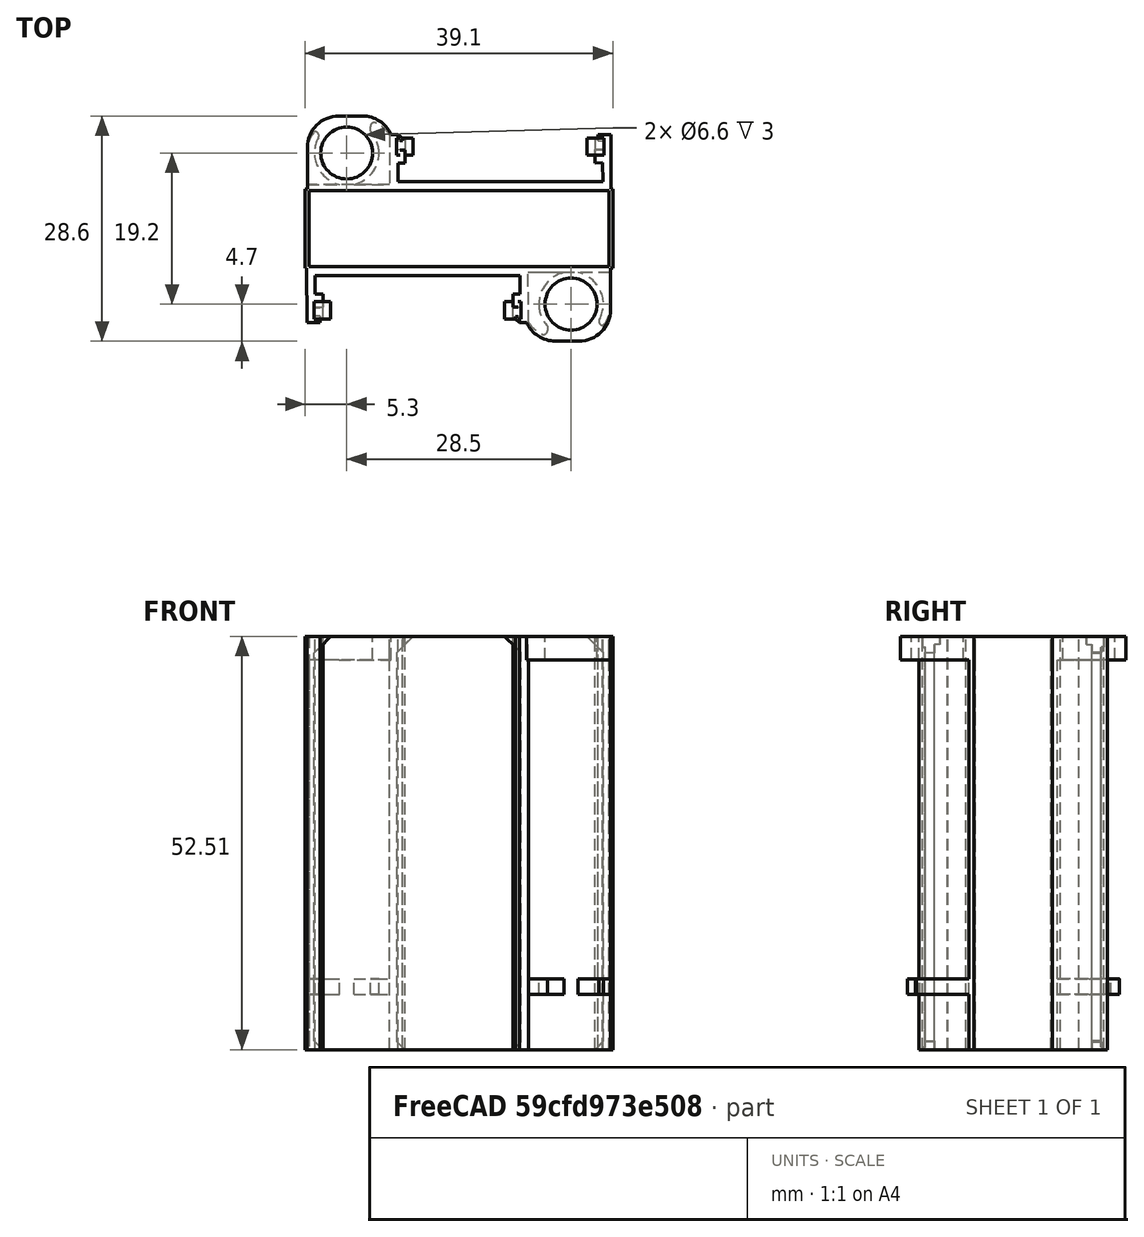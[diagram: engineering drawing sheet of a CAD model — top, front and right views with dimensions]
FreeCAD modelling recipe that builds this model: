
FCSTD DOCUMENT  (FreeCAD 0.18.4R)
Label: ArduinoClip3
License: All rights reserved
LicenseURL: http://en.wikipedia.org/wiki/All_rights_reserved
objects: Part::Fillet×12, Sketcher::SketchObject×10, PartDesign::Pad×10, Part::Box×10, Part::Cut×6, Part::Cylinder×4, Part::MultiFuse×3, Mesh::Feature×1
note: 65 computed .brp shape members not serialized (recipe doc carries the construction recipe); baked Part::Feature solids carry a one-line shape summary decoded from their .brp

FEATURE [Sketcher::SketchObject] Sketch
  MapMode = 5
  sketch-geometry (21):
    g0: LineSegment StartX=-18.4968 StartY=-10.0088 StartZ=0 EndX=7.53504 EndY=-10.0088 EndZ=0
    g1: LineSegment StartX=8.57388 StartY=-11.2005 StartZ=0 EndX=-19.5534 EndY=-11.2005 EndZ=0
    g2: LineSegment StartX=-17.6048 StartY=-6.00567 StartZ=0 EndX=-17.6048 EndY=-7.68179 EndZ=0
    g3: LineSegment StartX=8.57269 StartY=-4.05913 StartZ=0 EndX=8.57388 EndY=-11.2005 EndZ=0
    g4: LineSegment StartX=6.91065 StartY=-4.05913 StartZ=0 EndX=6.91356 EndY=-4.85559 EndZ=0
    g5: LineSegment StartX=6.91065 StartY=-4.05913 StartZ=0 EndX=8.57269 EndY=-4.05913 EndZ=0
    g6: LineSegment StartX=6.91356 StartY=-4.85559 StartZ=0 EndX=7.6386 EndY=-4.86736 EndZ=0
    g7: LineSegment StartX=7.6386 StartY=-4.86736 StartZ=0 EndX=7.64142 EndY=-5.99166 EndZ=0
    g8: LineSegment StartX=7.64142 StartY=-5.99166 StartZ=0 EndX=6.53466 EndY=-5.99604 EndZ=0
    g9: LineSegment StartX=6.53466 StartY=-5.99604 StartZ=0 EndX=6.53538 EndY=-7.65721 EndZ=0
    g10: LineSegment StartX=-17.6048 StartY=-6.00567 StartZ=0 EndX=-18.6255 EndY=-6.00154 EndZ=0
    g11: LineSegment StartX=-18.6255 StartY=-6.00154 StartZ=0 EndX=-18.62 EndY=-4.8031 EndZ=0
    g12: LineSegment StartX=-18.62 StartY=-4.8031 StartZ=0 EndX=-17.9262 EndY=-4.80553 EndZ=0
    g13: LineSegment StartX=-17.9262 StartY=-4.80553 StartZ=0 EndX=-17.9262 EndY=-4.48409 EndZ=0
    g14: LineSegment StartX=-17.9262 StartY=-4.48409 StartZ=0 EndX=-18.4601 EndY=-4.05553 EndZ=0
    g15: LineSegment StartX=-19.5659 StartY=-4.05361 StartZ=0 EndX=-19.5534 EndY=-11.2005 EndZ=0
    g16: LineSegment StartX=-17.6048 StartY=-7.68179 StartZ=0 EndX=-18.4968 EndY=-7.686 EndZ=0
    g17: LineSegment StartX=-18.4968 StartY=-7.686 StartZ=0 EndX=-18.4968 EndY=-10.0088 EndZ=0
    g18: LineSegment StartX=7.5169 StartY=-7.64985 StartZ=0 EndX=6.53538 EndY=-7.65721 EndZ=0
    g19: LineSegment StartX=7.53504 StartY=-10.0088 StartZ=0 EndX=7.5169 EndY=-7.64985 EndZ=0
    g20: LineSegment StartX=-19.5659 StartY=-4.05361 StartZ=0 EndX=-18.4601 EndY=-4.05553 EndZ=0
  constraints (24):
    c: Horizontal(g0)
    c: Horizontal(g1)
    c: Vertical(g2)
    c: Coincident(g1,g3)
    c: Coincident(g5,g4)
    c: Coincident(g4,g6)
    c: Coincident(g6,g7)
    c: Coincident(g7,g8)
    c: Coincident(g9,g8)
    c: Coincident(g5,g3)
    c: Coincident(g10,g2)
    c: Coincident(g10,g11)
    c: Coincident(g11,g12)
    c: Coincident(g12,g13)
    c: Coincident(g13,g14)
    c: Coincident(g15,g1)
    c: Coincident(g16,g2)
    c: Coincident(g16,g17)
    c: Coincident(g0,g17)
    c: Coincident(g9,g18)
    c: Coincident(g18,g19)
    c: Coincident(g0,g19)
    c: Coincident(g20,g15)
    c: Coincident(g20,g14)
FEATURE [PartDesign::Pad] Pad
  Length = 52.5
  Length2 = 100
  Profile = -> Sketch
  Type = 0
FEATURE [Sketcher::SketchObject] Sketch004
  MapMode = 5
  Placement = pos=(-11.64,-4.5,6.03) rot=(1,0,0;1.5708rad)
  sketch-geometry (3):
    g0: LineSegment StartX=-7.00166 StartY=-5.01077 StartZ=0 EndX=-6.98953 EndY=-6.02972 EndZ=0
    g1: LineSegment StartX=-6.98953 StartY=-6.02972 StartZ=0 EndX=-5.96627 EndY=-6.02972 EndZ=0
    g2: LineSegment StartX=-7.00166 StartY=-5.01077 StartZ=0 EndX=-5.96627 EndY=-6.02972 EndZ=0
  constraints (3):
    c: Coincident(g0,g1)
    c: Coincident(g2,g0)
    c: Coincident(g2,g1)
FEATURE [PartDesign::Pad] Pad004  label="stopper002"
  Length = 2.2
  Length2 = 100
  Placement = pos=(-11.64,-4.5,6.03) rot=(1,0,0;1.5708rad)
  Profile = -> Sketch004
  Type = 0
FEATURE [Sketcher::SketchObject] Sketch006
  MapMode = 5
  Placement = pos=(7.7,-4.5,0.03) rot=(1,0,0;1.5708rad)
  sketch-geometry (3):
    g0: LineSegment StartX=-0.009992 StartY=1.14657 StartZ=0 EndX=-0.005347 EndY=-0.027131 EndZ=0
    g1: LineSegment StartX=-0.005347 StartY=-0.027131 StartZ=0 EndX=-1.16636 EndY=-0.03134 EndZ=0
    g2: LineSegment StartX=-1.16636 StartY=-0.03134 StartZ=0 EndX=-0.009992 EndY=1.14657 EndZ=0
  constraints (3):
    c: Coincident(g0,g1)
    c: Coincident(g1,g2)
    c: Coincident(g2,g0)
FEATURE [PartDesign::Pad] Pad006  label="stopper003"
  Length = 2.2
  Length2 = 100
  Placement = pos=(7.7,-4.5,0.03) rot=(1,0,0;1.5708rad)
  Profile = -> Sketch006
  Type = 0
FEATURE [Sketcher::SketchObject] Sketch007
  MapMode = 5
  Placement = pos=(7.66,-4.5,50.5) rot=(1,0,0;1.5708rad)
  sketch-geometry (3):
    g0: LineSegment StartX=0.006942 StartY=2.00104 StartZ=0 EndX=-0.00277 EndY=-0.125835 EndZ=0
    g1: LineSegment StartX=-0.00277 StartY=-0.125835 StartZ=0 EndX=-2.12965 EndY=2.01075 EndZ=0
    g2: LineSegment StartX=-2.12965 StartY=2.01075 StartZ=0 EndX=0.006942 EndY=2.00104 EndZ=0
  constraints (3):
    c: Coincident(g0,g1)
    c: Coincident(g1,g2)
    c: Coincident(g2,g0)
FEATURE [Sketcher::SketchObject] Sketch008
  MapMode = 5
  Placement = pos=(-17.65,-4.5,50.5) rot=(1,0,0;1.5708rad)
  sketch-geometry (3):
    g0: LineSegment StartX=1.0898 StartY=1.99523 StartZ=0 EndX=-0.993398 EndY=-0.061924 EndZ=0
    g1: LineSegment StartX=-0.993398 StartY=-0.061924 StartZ=0 EndX=-0.997928 EndY=2.00119 EndZ=0
    g2: LineSegment StartX=-0.997928 StartY=2.00119 StartZ=0 EndX=1.0898 EndY=1.99523 EndZ=0
  constraints (3):
    c: Coincident(g0,g1)
    c: Coincident(g1,g2)
    c: Coincident(g2,g0)
FEATURE [PartDesign::Pad] Pad008  label="stopper001"
  Length = 2.2
  Length2 = 100
  Placement = pos=(-17.65,-4.5,50.5) rot=(1,0,0;1.5708rad)
  Profile = -> Sketch008
  Type = 0
FEATURE [Part::Box] Box002  label="Würfel"
  AttacherType = Attacher::AttachEngine3D
  Height = 2
  Length = 11
  Placement = pos=(-30,-11,7) rot=(0,0,1;0rad)
  Width = 9
FEATURE [Part::Cylinder] Cylinder  label="Zylinder"
  Angle = 360
  AttacherType = Attacher::AttachEngine3D
  Height = 10
  Placement = pos=(-25,-6.2,0) rot=(0,0,1;0rad)
  Radius = 4.1
FEATURE [Part::Cut] Cut002
  Base = -> Box002
  Tool = -> Cylinder
FEATURE [Part::Fillet] Fillet002
  Base = -> Cut002
  Edges = 1 edges r=4: [Edge12]
FEATURE [Part::Fillet] Fillet003  label="Antenne001"
  Base = -> Fillet002
  Edges = 1 edges r=4: [Edge9]
  Placement = pos=(0,-0.2,0) rot=(0,0,1;0rad)
FEATURE [PartDesign::Pad] Pad007  label="stopper004"
  Length = 2.2
  Length2 = 100
  Placement = pos=(7.66,-4.5,50.5) rot=(1,0,0;1.5708rad)
  Profile = -> Sketch007
  Type = 0
FEATURE [Part::Box] Box003  label="Würfel001"
  AttacherType = Attacher::AttachEngine3D
  Height = 3
  Length = 11
  Placement = pos=(-30,-11,7) rot=(0,0,1;0rad)
  Width = 9.5
FEATURE [Part::Cylinder] Cylinder001  label="Zylinder001"
  Angle = 360
  AttacherType = Attacher::AttachEngine3D
  Height = 10
  Placement = pos=(-25,-6.2,0) rot=(0,0,1;0rad)
  Radius = 3.3
FEATURE [Part::Cut] Cut003
  Base = -> Box003
  Placement = pos=(0,0,42.5) rot=(0,0,1;0rad)
  Tool = -> Cylinder001
FEATURE [Part::Fillet] Fillet004
  Base = -> Cut003
  Edges = 1 edges r=4: [Edge12]
FEATURE [Part::Fillet] Fillet005  label="Antenne002"
  Base = -> Fillet004
  Edges = 1 edges r=4: [Edge9]
  Placement = pos=(0,-0.2,0) rot=(0,0,1;0rad)
FEATURE [Part::Box] Box  label="AntenneBoden"
  AttacherType = Attacher::AttachEngine3D
  Height = 50
  Length = 11
  Placement = pos=(-30,-11.2,0) rot=(0,0,1;0rad)
  Width = 0.8
FEATURE [Part::Box] Box004  label="Würfel003"
  AttacherType = Attacher::AttachEngine3D
  Height = 5
  Length = 8
  Placement = pos=(-30,-3.7,6.5) rot=(0,0,1;0rad)
  Width = 5
FEATURE [Part::Cut] Cut
  Base = -> Fillet003
  Tool = -> Box004
FEATURE [Part::Fillet] Fillet
  Base = -> Cut
  Edges = 1 edges r=0.5: [Edge12]
FEATURE [Part::Fillet] Fillet006
  Base = -> Fillet
  Edges = 1 edges r=0.5: [Edge26]
FEATURE [Part::MultiFuse] Fusion
  Shapes = -> [Pad,Fillet005,Pad004,Pad006,Pad008,Pad007,Box,Fillet006]
FEATURE [Part::Box] Box005  label="Würfel004"
  AttacherType = Attacher::AttachEngine3D
  Height = 2
  Length = 11
  Placement = pos=(-30,-11,7) rot=(0,0,1;0rad)
  Width = 9
FEATURE [Sketcher::SketchObject] Sketch009
  MapMode = 5
  Placement = pos=(-11.64,-4.5,6.03) rot=(1,0,0;1.5708rad)
  sketch-geometry (3):
    g0: LineSegment StartX=-7.00166 StartY=-5.01077 StartZ=0 EndX=-6.98953 EndY=-6.02972 EndZ=0
    g1: LineSegment StartX=-6.98953 StartY=-6.02972 StartZ=0 EndX=-5.96627 EndY=-6.02972 EndZ=0
    g2: LineSegment StartX=-7.00166 StartY=-5.01077 StartZ=0 EndX=-5.96627 EndY=-6.02972 EndZ=0
  constraints (3):
    c: Coincident(g0,g1)
    c: Coincident(g2,g0)
    c: Coincident(g2,g1)
FEATURE [PartDesign::Pad] Pad010  label="stopper005"
  Length = 2.2
  Length2 = 100
  Placement = pos=(-11.64,-4.5,6.03) rot=(1,0,0;1.5708rad)
  Profile = -> Sketch009
  Type = 0
FEATURE [Sketcher::SketchObject] Sketch010
  MapMode = 5
  Placement = pos=(7.7,-4.5,0.03) rot=(1,0,0;1.5708rad)
  sketch-geometry (3):
    g0: LineSegment StartX=-0.009992 StartY=1.14657 StartZ=0 EndX=-0.005347 EndY=-0.027131 EndZ=0
    g1: LineSegment StartX=-0.005347 StartY=-0.027131 StartZ=0 EndX=-1.16636 EndY=-0.03134 EndZ=0
    g2: LineSegment StartX=-1.16636 StartY=-0.03134 StartZ=0 EndX=-0.009992 EndY=1.14657 EndZ=0
  constraints (3):
    c: Coincident(g0,g1)
    c: Coincident(g1,g2)
    c: Coincident(g2,g0)
FEATURE [PartDesign::Pad] Pad011  label="stopper006"
  Length = 2.2
  Length2 = 100
  Placement = pos=(7.7,-4.5,0.03) rot=(1,0,0;1.5708rad)
  Profile = -> Sketch010
  Type = 0
FEATURE [Part::Box] Box006  label="Würfel005"
  AttacherType = Attacher::AttachEngine3D
  Height = 3
  Length = 11
  Placement = pos=(-30,-11,7) rot=(0,0,1;0rad)
  Width = 9.5
FEATURE [Part::Box] Box007  label="AntenneBoden001"
  AttacherType = Attacher::AttachEngine3D
  Height = 50
  Length = 11
  Placement = pos=(-30,-11.2,0) rot=(0,0,1;0rad)
  Width = 0.8
FEATURE [Sketcher::SketchObject] Sketch011
  MapMode = 5
  Placement = pos=(7.66,-4.5,50.5) rot=(1,0,0;1.5708rad)
  sketch-geometry (3):
    g0: LineSegment StartX=0.006942 StartY=2.00104 StartZ=0 EndX=-0.00277 EndY=-0.125835 EndZ=0
    g1: LineSegment StartX=-0.00277 StartY=-0.125835 StartZ=0 EndX=-2.12965 EndY=2.01075 EndZ=0
    g2: LineSegment StartX=-2.12965 StartY=2.01075 StartZ=0 EndX=0.006942 EndY=2.00104 EndZ=0
  constraints (3):
    c: Coincident(g0,g1)
    c: Coincident(g1,g2)
    c: Coincident(g2,g0)
FEATURE [PartDesign::Pad] Pad013  label="stopper008"
  Length = 2.2
  Length2 = 100
  Placement = pos=(7.66,-4.5,50.5) rot=(1,0,0;1.5708rad)
  Profile = -> Sketch011
  Type = 0
FEATURE [Part::Box] Box008  label="Würfel006"
  AttacherType = Attacher::AttachEngine3D
  Height = 5
  Length = 8
  Placement = pos=(-30,-3.7,6.5) rot=(0,0,1;0rad)
  Width = 5
FEATURE [Sketcher::SketchObject] Sketch012
  MapMode = 5
  sketch-geometry (21):
    g0: LineSegment StartX=-18.4968 StartY=-10.0088 StartZ=0 EndX=7.53504 EndY=-10.0088 EndZ=0
    g1: LineSegment StartX=8.57388 StartY=-11.2005 StartZ=0 EndX=-19.5534 EndY=-11.2005 EndZ=0
    g2: LineSegment StartX=-17.6048 StartY=-6.00567 StartZ=0 EndX=-17.6048 EndY=-7.68179 EndZ=0
    g3: LineSegment StartX=8.57269 StartY=-4.05913 StartZ=0 EndX=8.57388 EndY=-11.2005 EndZ=0
    g4: LineSegment StartX=6.91065 StartY=-4.05913 StartZ=0 EndX=6.91356 EndY=-4.85559 EndZ=0
    g5: LineSegment StartX=6.91065 StartY=-4.05913 StartZ=0 EndX=8.57269 EndY=-4.05913 EndZ=0
    g6: LineSegment StartX=6.91356 StartY=-4.85559 StartZ=0 EndX=7.6386 EndY=-4.86736 EndZ=0
    g7: LineSegment StartX=7.6386 StartY=-4.86736 StartZ=0 EndX=7.64142 EndY=-5.99166 EndZ=0
    g8: LineSegment StartX=7.64142 StartY=-5.99166 StartZ=0 EndX=6.53466 EndY=-5.99604 EndZ=0
    g9: LineSegment StartX=6.53466 StartY=-5.99604 StartZ=0 EndX=6.53538 EndY=-7.65721 EndZ=0
    g10: LineSegment StartX=-17.6048 StartY=-6.00567 StartZ=0 EndX=-18.6255 EndY=-6.00154 EndZ=0
    g11: LineSegment StartX=-18.6255 StartY=-6.00154 StartZ=0 EndX=-18.62 EndY=-4.8031 EndZ=0
    g12: LineSegment StartX=-18.62 StartY=-4.8031 StartZ=0 EndX=-17.9262 EndY=-4.80553 EndZ=0
    g13: LineSegment StartX=-17.9262 StartY=-4.80553 StartZ=0 EndX=-17.9262 EndY=-4.48409 EndZ=0
    g14: LineSegment StartX=-17.9262 StartY=-4.48409 StartZ=0 EndX=-18.4601 EndY=-4.05553 EndZ=0
    g15: LineSegment StartX=-19.5659 StartY=-4.05361 StartZ=0 EndX=-19.5534 EndY=-11.2005 EndZ=0
    g16: LineSegment StartX=-17.6048 StartY=-7.68179 StartZ=0 EndX=-18.4968 EndY=-7.686 EndZ=0
    g17: LineSegment StartX=-18.4968 StartY=-7.686 StartZ=0 EndX=-18.4968 EndY=-10.0088 EndZ=0
    g18: LineSegment StartX=7.5169 StartY=-7.64985 StartZ=0 EndX=6.53538 EndY=-7.65721 EndZ=0
    g19: LineSegment StartX=7.53504 StartY=-10.0088 StartZ=0 EndX=7.5169 EndY=-7.64985 EndZ=0
    g20: LineSegment StartX=-19.5659 StartY=-4.05361 StartZ=0 EndX=-18.4601 EndY=-4.05553 EndZ=0
  constraints (24):
    c: Horizontal(g0)
    c: Horizontal(g1)
    c: Vertical(g2)
    c: Coincident(g1,g3)
    c: Coincident(g5,g4)
    c: Coincident(g4,g6)
    c: Coincident(g6,g7)
    c: Coincident(g7,g8)
    c: Coincident(g9,g8)
    c: Coincident(g5,g3)
    c: Coincident(g10,g2)
    c: Coincident(g10,g11)
    c: Coincident(g11,g12)
    c: Coincident(g12,g13)
    c: Coincident(g13,g14)
    c: Coincident(g15,g1)
    c: Coincident(g16,g2)
    c: Coincident(g16,g17)
    c: Coincident(g0,g17)
    c: Coincident(g9,g18)
    c: Coincident(g18,g19)
    c: Coincident(g0,g19)
    c: Coincident(g20,g15)
    c: Coincident(g20,g14)
FEATURE [PartDesign::Pad] Pad009
  Length = 52.5
  Length2 = 100
  Profile = -> Sketch012
  Type = 0
FEATURE [Part::Cylinder] Cylinder002  label="Zylinder002"
  Angle = 360
  AttacherType = Attacher::AttachEngine3D
  Height = 10
  Placement = pos=(-25,-6.2,0) rot=(0,0,1;0rad)
  Radius = 4.1
FEATURE [Part::Cut] Cut006
  Base = -> Box005
  Tool = -> Cylinder002
FEATURE [Part::Fillet] Fillet009
  Base = -> Cut006
  Edges = 1 edges r=4: [Edge12]
FEATURE [Part::Fillet] Fillet010  label="Antenne004"
  Base = -> Fillet009
  Edges = 1 edges r=4: [Edge9]
  Placement = pos=(0,-0.2,0) rot=(0,0,1;0rad)
FEATURE [Part::Cut] Cut004
  Base = -> Fillet010
  Tool = -> Box008
FEATURE [Sketcher::SketchObject] Sketch013
  MapMode = 5
  Placement = pos=(-17.65,-4.5,50.5) rot=(1,0,0;1.5708rad)
  sketch-geometry (3):
    g0: LineSegment StartX=1.0898 StartY=1.99523 StartZ=0 EndX=-0.993398 EndY=-0.061924 EndZ=0
    g1: LineSegment StartX=-0.993398 StartY=-0.061924 StartZ=0 EndX=-0.997928 EndY=2.00119 EndZ=0
    g2: LineSegment StartX=-0.997928 StartY=2.00119 StartZ=0 EndX=1.0898 EndY=1.99523 EndZ=0
  constraints (3):
    c: Coincident(g0,g1)
    c: Coincident(g1,g2)
    c: Coincident(g2,g0)
FEATURE [PartDesign::Pad] Pad012  label="stopper007"
  Length = 2.2
  Length2 = 100
  Placement = pos=(-17.65,-4.5,50.5) rot=(1,0,0;1.5708rad)
  Profile = -> Sketch013
  Type = 0
FEATURE [Part::Cylinder] Cylinder003  label="Zylinder003"
  Angle = 360
  AttacherType = Attacher::AttachEngine3D
  Height = 10
  Placement = pos=(-25,-6.2,0) rot=(0,0,1;0rad)
  Radius = 3.3
FEATURE [Part::Cut] Cut005
  Base = -> Box006
  Placement = pos=(0,0,42.5) rot=(0,0,1;0rad)
  Tool = -> Cylinder003
FEATURE [Part::Fillet] Fillet007
  Base = -> Cut005
  Edges = 1 edges r=4: [Edge12]
FEATURE [Part::Fillet] Fillet008  label="Antenne003"
  Base = -> Fillet007
  Edges = 1 edges r=4: [Edge9]
  Placement = pos=(0,-0.2,0) rot=(0,0,1;0rad)
FEATURE [Part::Fillet] Fillet011
  Base = -> Cut004
  Edges = 1 edges r=0.5: [Edge12]
FEATURE [Part::Fillet] Fillet012
  Base = -> Fillet011
  Edges = 1 edges r=0.5: [Edge26]
FEATURE [Part::MultiFuse] Fusion001
  Placement = pos=(-21.5,-32,0) rot=(0,0,1;3.14159rad)
  Shapes = -> [Pad009,Fillet008,Pad010,Pad011,Pad012,Pad013,Box007,Fillet012]
FEATURE [Part::Box] Box009  label="Würfel007"
  AttacherType = Attacher::AttachEngine3D
  Height = 52.5
  Length = 0.5
  Placement = pos=(8.3,-21,0) rot=(0,0,1;0rad)
  Width = 10
FEATURE [Part::Box] Box010  label="Würfel008"
  AttacherType = Attacher::AttachEngine3D
  Height = 52.5
  Length = 0.5
  Placement = pos=(-30.3,-21,0) rot=(0,0,1;0rad)
  Width = 10
FEATURE [Part::MultiFuse] Fusion002
  Shapes = -> [Fusion,Fusion001,Box009,Box010]
FEATURE [Mesh::Feature] Mesh  label="Fusion002 (Meshed)"
